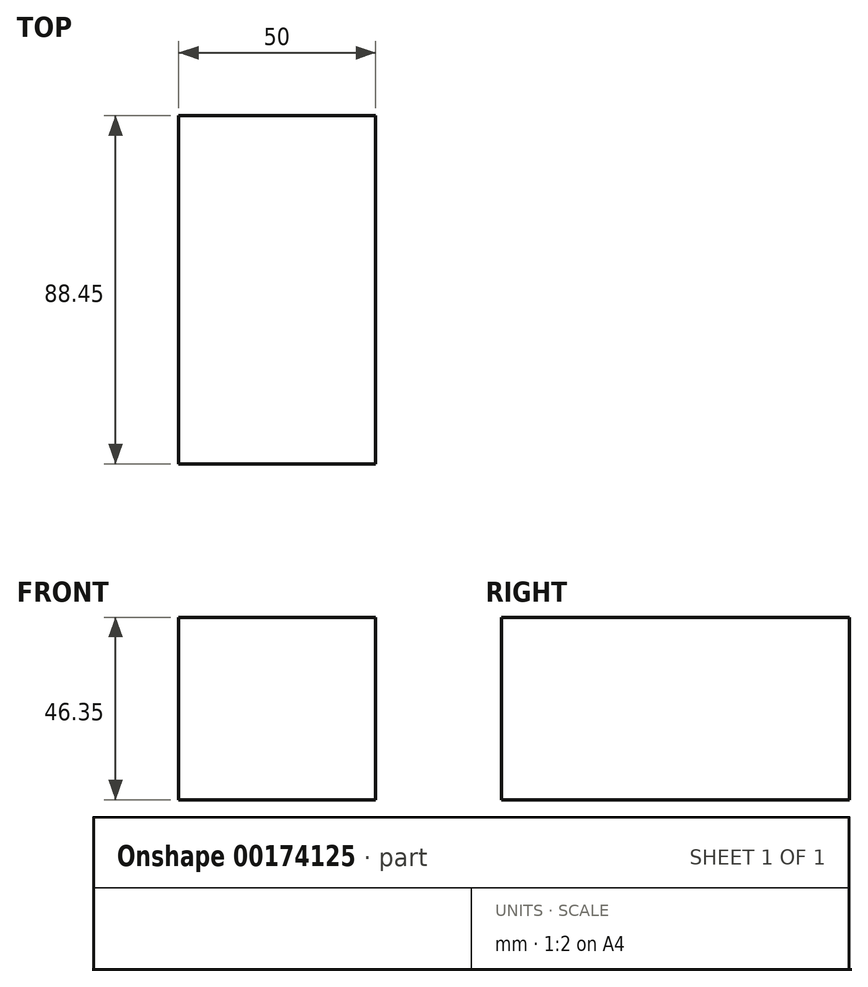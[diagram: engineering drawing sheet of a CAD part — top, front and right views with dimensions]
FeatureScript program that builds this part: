
annotation { "Feature Type Name" : "Feature", "Feature Type Description" : "" }
export const myFeature = defineFeature(function(context is Context, id is Id, definition is map)
    precondition{}
    {
        {
            var Q0;
            Q0=qCreatedBy(makeId("Front.planeOp"),FACE);
            var sketch = newSketch(context, id + "F1", { "sketchPlane" : qUnion([Q0])});
            skLineSegment(sketch, "E0.bottom", {"start": v(23.1, 18.86) * mm, "end": v(73.1, 18.86) * mm});
            skLineSegment(sketch, "E0.top", {"start": v(23.1, -27.5) * mm, "end": v(73.1, -27.5) * mm});
            skLineSegment(sketch, "E0.left", {"start": v(23.1, 18.86) * mm, "end": v(23.1, -27.5) * mm});
            skLineSegment(sketch, "E0.right", {"start": v(73.1, 18.86) * mm, "end": v(73.1, -27.5) * mm});
            skSolve(sketch);
        }
        {
            var Q0;
            Q0=makeQuery(id+"F1.imprint","IMPRINT",FACE,{"disambiguationData":[TD([[makeQuery(id+"F1.imprint","IMPRINT",EDGE,{"derivedFrom":sQuery(id+"F1.wireOp",EDGE,"E0.bottom")}),-1.0]])]});
            extrude(context, id + "F0", {"entities" : qUnion([Q0]), "depth" : 88.45 * mm});
        }
    });
